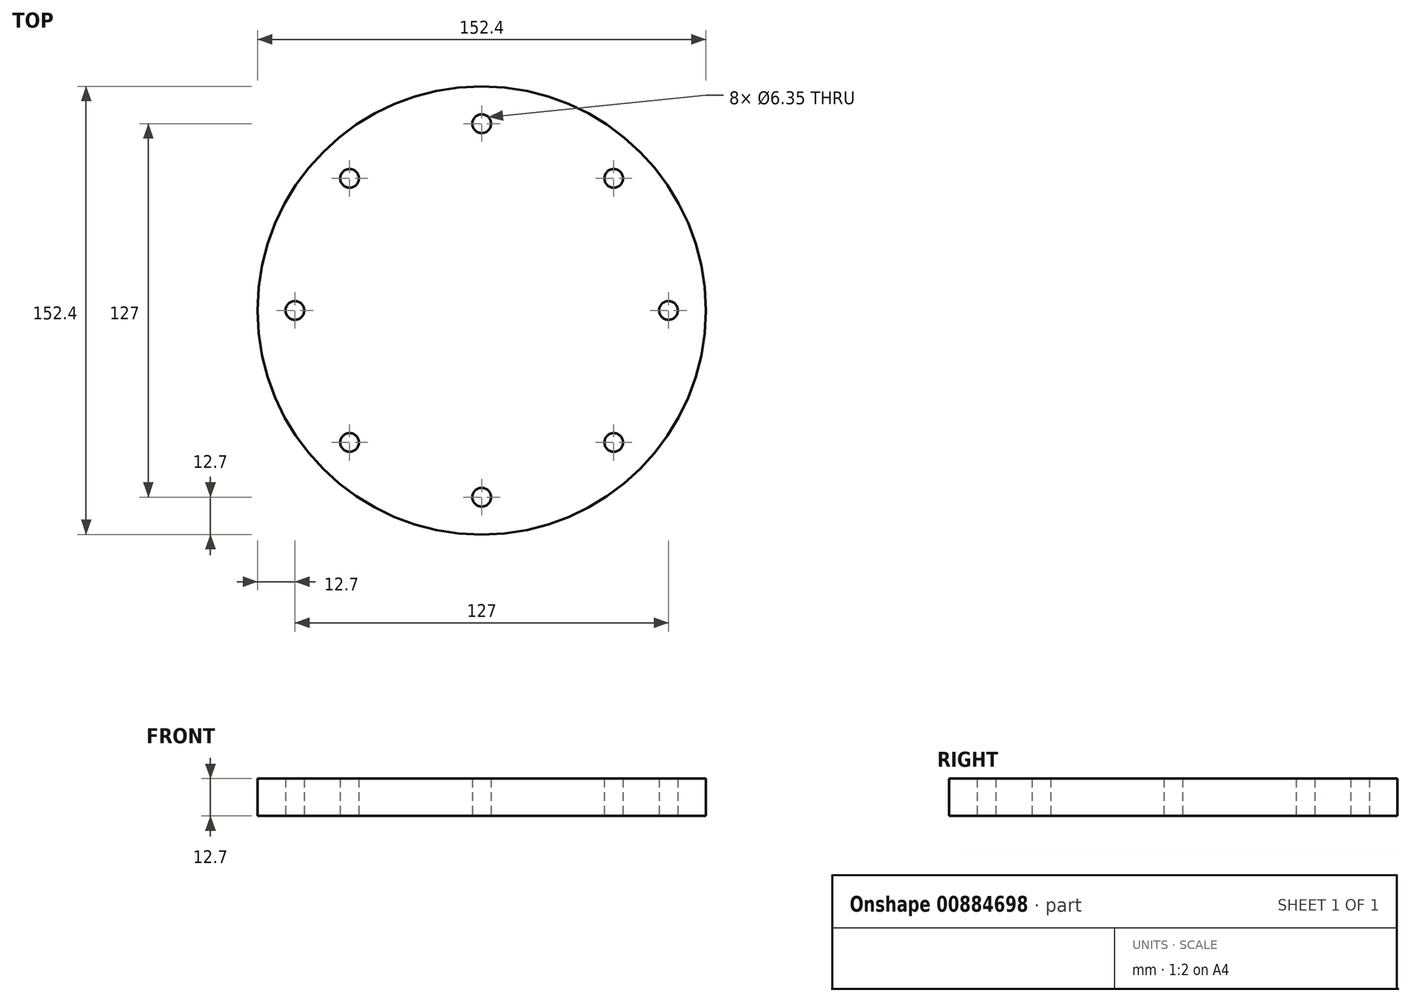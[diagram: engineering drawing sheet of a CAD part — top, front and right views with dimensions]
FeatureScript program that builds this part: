
annotation { "Feature Type Name" : "Feature", "Feature Type Description" : "" }
export const myFeature = defineFeature(function(context is Context, id is Id, definition is map)
    precondition{}
    {
        {
            var Q0;
            Q0=qCreatedBy(makeId("Top.planeOp"),FACE);
            var sketch = newSketch(context, id + "F0", { "sketchPlane" : qUnion([Q0])});
            skCircle(sketch, "E0", {"center": v(0, 0) * mm, "radius": 76.2 * mm});
            skCircle(sketch, "E1", {"center": v(0, 0) * mm, "radius": 63.5 * mm});
            skCircle(sketch, "E2", {"center": v(0, 63.5) * mm, "radius": 3.18 * mm});
            skCircle(sketch, "E3", {"center": v(63.5, 0) * mm, "radius": 3.18 * mm});
            skCircle(sketch, "E4", {"center": v(-63.5, 0) * mm, "radius": 3.18 * mm});
            skCircle(sketch, "E5", {"center": v(0, -63.5) * mm, "radius": 3.18 * mm});
            skLineSegment(sketch, "E6", {"start": v(0, 0) * mm, "end": v(-44.9, 44.9) * mm});
            skLineSegment(sketch, "E7", {"start": v(0, 0) * mm, "end": v(44.9, -44.9) * mm});
            skLineSegment(sketch, "E8", {"start": v(0, 0) * mm, "end": v(44.9, 44.9) * mm});
            skLineSegment(sketch, "E9", {"start": v(0, 0) * mm, "end": v(-44.9, -44.9) * mm});
            skCircle(sketch, "E10", {"center": v(44.9, -44.9) * mm, "radius": 3.18 * mm});
            skCircle(sketch, "E11", {"center": v(44.9, 44.9) * mm, "radius": 3.18 * mm});
            skCircle(sketch, "E12", {"center": v(-44.9, 44.9) * mm, "radius": 3.18 * mm});
            skCircle(sketch, "E13", {"center": v(-44.9, -44.9) * mm, "radius": 3.18 * mm});
            skSolve(sketch);
        }
        {
            var Q0;
            Q0 = qSketchRegion(id + "F0", true);
            var Q1;
            {var subQ1=sQuery(id+"F0.wireOp",EDGE,"E1");var subQ10=sQuery(id+"F0.wireOp",EDGE,"E11");var subQ11=makeQuery(id+"F0.imprint","INTERSECT",VERTEX,{"disambiguationData":[OD(1.0)],"derivedFrom":[subQ1,subQ10]});Q1=makeQuery(id+"F0.imprint","IMPRINT",FACE,{"disambiguationData":[TD([[makeQuery(id+"F0.imprint","IMPRINT",EDGE,{"disambiguationData":[TD([[subQ11,-1.0]])],"derivedFrom":subQ1}),1.0]])]});}
            var Q2;
            {var subQ1=sQuery(id+"F0.wireOp",EDGE,"E1");var subQ6=sQuery(id+"F0.wireOp",EDGE,"E12");var subQ7=makeQuery(id+"F0.imprint","INTERSECT",VERTEX,{"disambiguationData":[OD(1.0)],"derivedFrom":[subQ1,subQ6]});Q2=makeQuery(id+"F0.imprint","IMPRINT",FACE,{"disambiguationData":[TD([[makeQuery(id+"F0.imprint","IMPRINT",EDGE,{"disambiguationData":[TD([[subQ7,-1.0]])],"derivedFrom":subQ1}),1.0]])]});}
            var Q3;
            {var subQ1=sQuery(id+"F0.wireOp",EDGE,"E1");var subQ10=sQuery(id+"F0.wireOp",EDGE,"E13");var subQ11=makeQuery(id+"F0.imprint","INTERSECT",VERTEX,{"disambiguationData":[OD(1.0)],"derivedFrom":[subQ1,subQ10]});Q3=makeQuery(id+"F0.imprint","IMPRINT",FACE,{"disambiguationData":[TD([[makeQuery(id+"F0.imprint","IMPRINT",EDGE,{"disambiguationData":[TD([[subQ11,-1.0]])],"derivedFrom":subQ1}),1.0]])]});}
            var Q4;
            {var subQ1=sQuery(id+"F0.wireOp",EDGE,"E1");var subQ4=sQuery(id+"F0.wireOp",EDGE,"E11");var subQ5=makeQuery(id+"F0.imprint","INTERSECT",VERTEX,{"disambiguationData":[OD(0.0)],"derivedFrom":[subQ1,subQ4]});Q4=makeQuery(id+"F0.imprint","IMPRINT",FACE,{"disambiguationData":[TD([[makeQuery(id+"F0.imprint","IMPRINT",EDGE,{"disambiguationData":[TD([[subQ5,1.0]])],"derivedFrom":subQ1}),1.0]])]});}
            extrude(context, id + "F1", {"entities" : qUnion([Q0, Q1, Q2, Q3, Q4]), "depth" : 12.7 * mm, "offsetDistance" : 25.4 * mm});
        }
    });
